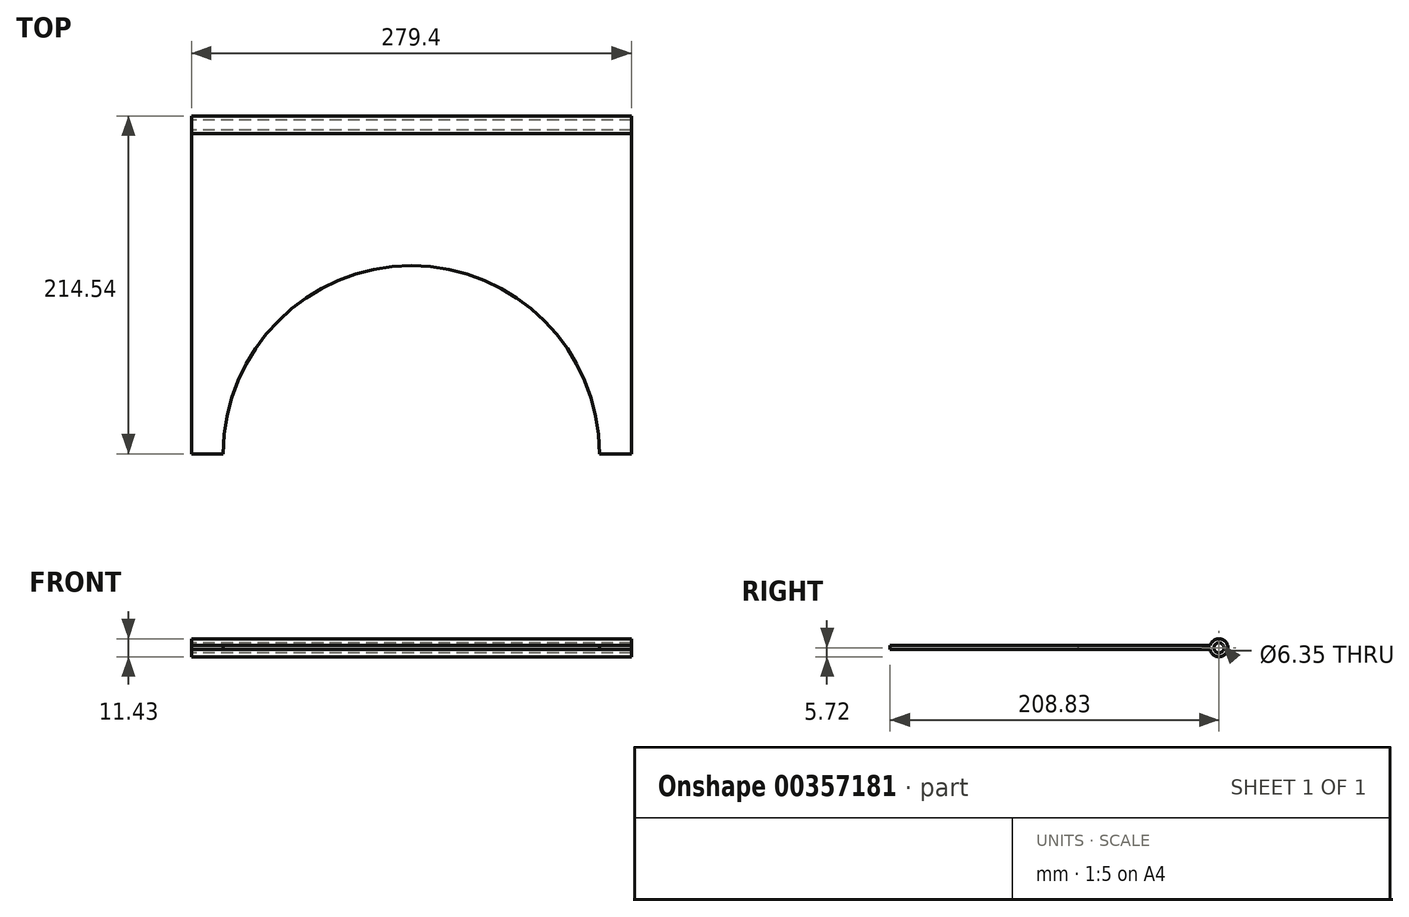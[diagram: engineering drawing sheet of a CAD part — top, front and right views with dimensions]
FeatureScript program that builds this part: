
annotation { "Feature Type Name" : "Feature", "Feature Type Description" : "" }
export const myFeature = defineFeature(function(context is Context, id is Id, definition is map)
    precondition{}
    {
        {
            var Q0;
            Q0=qCreatedBy(makeId("Right.planeOp"),FACE);
            var sketch = newSketch(context, id + "F0", { "sketchPlane" : qUnion([Q0])});
            skCircle(sketch, "E0", {"center": v(0, 0) * mm, "radius": 3.18 * mm});
            skLineSegment(sketch, "E1", {"start": v(-5.54, 1.41) * mm, "end": v(-208.83, 1.41) * mm});
            skLineSegment(sketch, "E2", {"start": v(-5.6, -1.13) * mm, "end": v(-208.83, -1.13) * mm});
            skLineSegment(sketch, "E3", {"start": v(-208.83, -1.13) * mm, "end": v(-208.83, 1.41) * mm});
            skLineSegment(sketch, "E4", {"start": v(-5.63, -1.13) * mm, "end": v(-5.63, -1.13) * mm});
            skPoint(sketch, "E5.orphan", {"position": v(-5.63, 1.41) * mm});
            skArc(sketch, "E6", {"start": v(-5.6, -1.13) * mm, "mid": v(5.71, -0.15) * mm, "end": v(-5.54, 1.41) * mm});
            skSolve(sketch);
        }
        {
            var Q0;
            Q0 = qSketchRegion(id + "F0", true);
            extrude(context, id + "F1", {"entities" : qUnion([Q0]), "depth" : 279.4 * mm});
        }
        {
            var Q0;
            Q0=makeQuery(id+"F1.opExtrude","SWEPT_FACE",FACE,{"disambiguationData":[OSD([sQuery(id+"F0.wireOp",EDGE,"E1")])]});
            var sketch = newSketch(context, id + "F2", { "sketchPlane" : qUnion([Q0])});
            skArc(sketch, "E7", {"start": v(259.16, -208.83) * mm, "mid": v(139.7, -89.37) * mm, "end": v(20.24, -208.83) * mm});
            skSolve(sketch);
        }
        {
            var Q0;
            {var subQ0=sQuery(id+"F2.wireOp",EDGE,"E7");var subQ1=makeQuery(id+"F1.opExtrude","SWEPT_EDGE",EDGE,{"disambiguationData":[OSD([sQuery(id+"F0.wireOp",EDGE,"E1"),sQuery(id+"F0.wireOp",EDGE,"E3")])]});var subQ2=makeQuery(id+"F2.imprint","INTERSECT",VERTEX,{"disambiguationData":[OD(0.0)],"derivedFrom":[subQ1,subQ0]});Q0=makeQuery(id+"F2.imprint","IMPRINT",FACE,{"disambiguationData":[TD([[makeQuery(id+"F2.imprint","IMPRINT",EDGE,{"disambiguationData":[TD([[subQ2,1.0]])],"derivedFrom":subQ0}),1.0]])]});}
            extrude(context, id + "F3", {"entities" : qUnion([Q0]), "operationType" : NewBodyOperationType.REMOVE, "oppositeDirection" : true, "depth" : 25.4 * mm});
        }
    });
